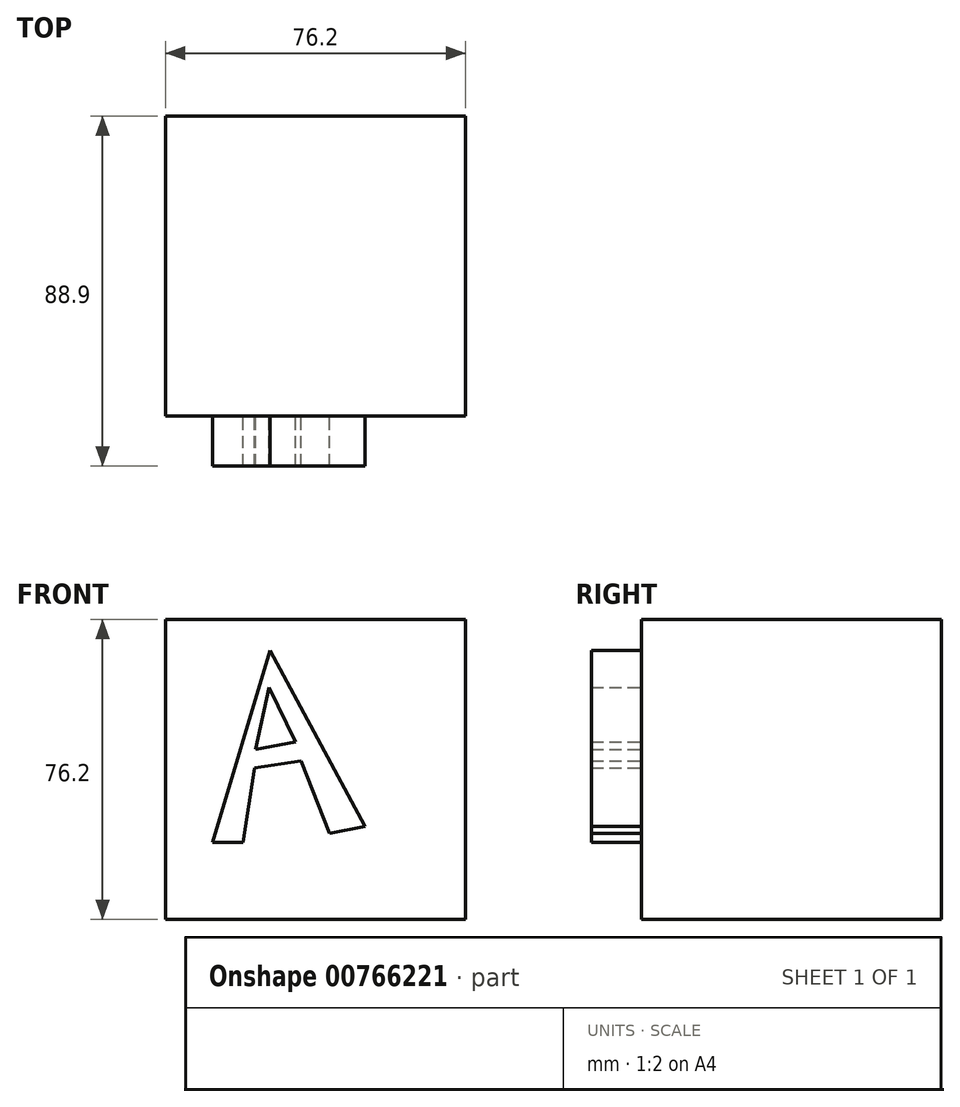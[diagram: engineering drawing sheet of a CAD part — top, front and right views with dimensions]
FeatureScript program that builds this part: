
annotation { "Feature Type Name" : "Feature", "Feature Type Description" : "" }
export const myFeature = defineFeature(function(context is Context, id is Id, definition is map)
    precondition{}
    {
        {
            var Q0;
            Q0=qCreatedBy(makeId("Front.planeOp"),FACE);
            var sketch = newSketch(context, id + "F0", { "sketchPlane" : qUnion([Q0])});
            skLineSegment(sketch, "E0.bottom", {"start": v(-39.1, 31.95) * mm, "end": v(37.1, 31.95) * mm});
            skLineSegment(sketch, "E0.top", {"start": v(-39.1, -44.25) * mm, "end": v(37.1, -44.25) * mm});
            skLineSegment(sketch, "E0.left", {"start": v(-39.1, 31.95) * mm, "end": v(-39.1, -44.25) * mm});
            skLineSegment(sketch, "E0.right", {"start": v(37.1, 31.95) * mm, "end": v(37.1, -44.25) * mm});
            skSolve(sketch);
        }
        {
            var Q0;
            Q0=makeQuery(id+"F0.imprint","IMPRINT",FACE,{"disambiguationData":[TD([[makeQuery(id+"F0.imprint","IMPRINT",EDGE,{"derivedFrom":sQuery(id+"F0.wireOp",EDGE,"E0.bottom")}),-1.0]])]});
            extrude(context, id + "F1", {"entities" : qUnion([Q0]), "depth" : 76.2 * mm, "offsetDistance" : 25.4 * mm});
        }
        {
            var Q0;
            Q0=makeQuery(id+"F1.opExtrude","CAP_FACE",FACE,{"disambiguationData":[OSD([sQuery(id+"F0.wireOp",EDGE,"E0.bottom"),sQuery(id+"F0.wireOp",EDGE,"E0.top"),sQuery(id+"F0.wireOp",EDGE,"E0.left"),sQuery(id+"F0.wireOp",EDGE,"E0.right")])],"isStart":false});
            var sketch = newSketch(context, id + "F2", { "sketchPlane" : qUnion([Q0])});
            skLineSegment(sketch, "E1", {"start": v(-27.14, -24.63) * mm, "end": v(-19.38, -24.63) * mm});
            skLineSegment(sketch, "E2", {"start": v(-19.38, -24.63) * mm, "end": v(-16.51, -5.77) * mm});
            skLineSegment(sketch, "E3", {"start": v(-27.14, -24.63) * mm, "end": v(-12.61, 24.05) * mm});
            skLineSegment(sketch, "E4", {"start": v(-12.61, 24.05) * mm, "end": v(11.52, -20.65) * mm});
            skLineSegment(sketch, "E5", {"start": v(11.52, -20.65) * mm, "end": v(2.5, -22.38) * mm});
            skLineSegment(sketch, "E6", {"start": v(2.5, -22.38) * mm, "end": v(-4.64, -3.98) * mm});
            skLineSegment(sketch, "E7", {"start": v(-4.64, -3.98) * mm, "end": v(-16.51, -5.77) * mm});
            skLineSegment(sketch, "E8", {"start": v(-16.28, -1.04) * mm, "end": v(-6.11, 0.9) * mm});
            skLineSegment(sketch, "E9", {"start": v(-6.11, 0.9) * mm, "end": v(-12.86, 14.72) * mm});
            skLineSegment(sketch, "E10", {"start": v(-12.86, 14.72) * mm, "end": v(-16.28, -1.04) * mm});
            skSolve(sketch);
        }
        {
            var Q0;
            Q0=makeQuery(id+"F2.imprint","IMPRINT",FACE,{"disambiguationData":[TD([[makeQuery(id+"F2.imprint","IMPRINT",EDGE,{"derivedFrom":sQuery(id+"F2.wireOp",EDGE,"E1")}),1.0]])]});
            extrude(context, id + "F3", {"entities" : qUnion([Q0]), "operationType" : NewBodyOperationType.ADD, "depth" : 12.7 * mm, "offsetDistance" : 25.4 * mm});
        }
    });
